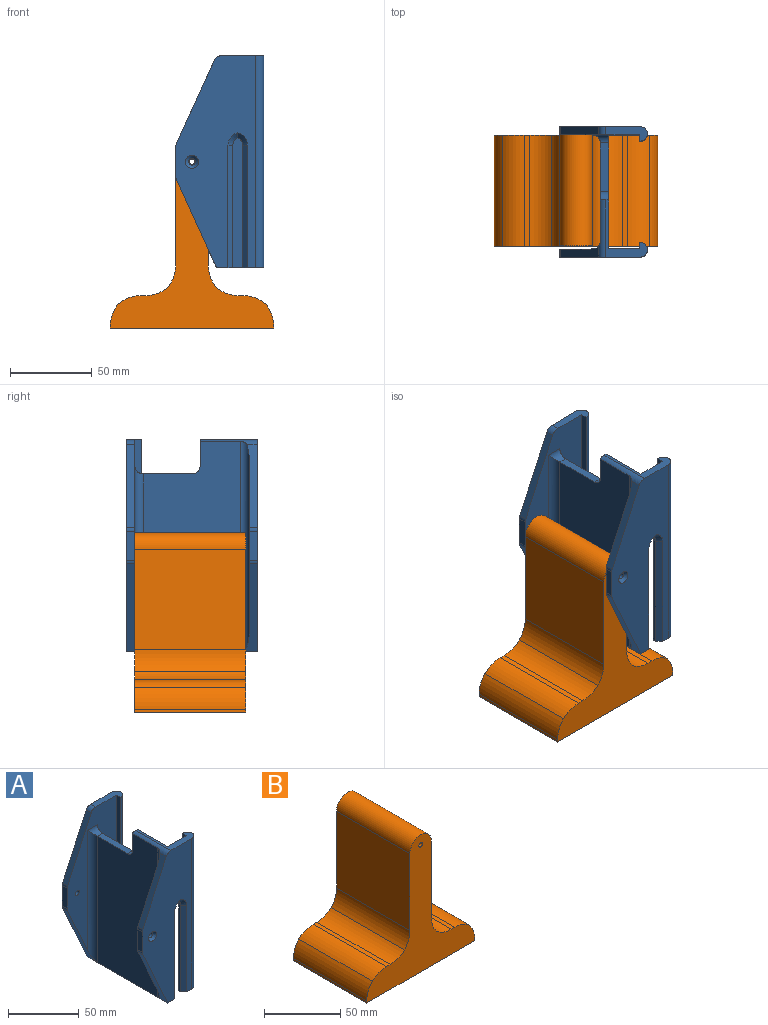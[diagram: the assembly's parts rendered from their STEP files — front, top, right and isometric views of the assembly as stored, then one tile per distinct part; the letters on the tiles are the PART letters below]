
ASSEMBLY  parts=2 mates=1
PART A: 47 faces, bbox 54.7x80.8x130.8 mm
  f0: plane 80x28.98mm, normal (0,0,-1), area 549.8mm2, adj f1,f3,f6,f9,f11,f12,f13,f16
  f1: plane 130x19mm, normal (0,1,0), area 2000.2mm2, adj f0,f7,f8,f11,f14,f23,f24,f25
  f2: plane 25.76x9mm, normal (0,0,1), area 138.2mm2, adj f6,f12,f13,f35,f39,f40
  f3: plane 128.83x60mm, normal (-1,0,0), area 7041mm2, adj f0,f21,f22,f27,f29,f30,f31
  f4: plane 17.83x5mm, normal (-1,0,0), area 89.2mm2, adj f9,f10,f32,f33
  f5: plane 17.83x5mm, normal (-1,0,0), area 89.2mm2, adj f6,f12,f34,f36
  f6: plane 130x49mm, normal (0,1,0), area 4942.8mm2, adj f0,f2,f5,f16,f17,f34,f35,f36
  f7: plane 35x25.76mm, normal (0,0,1), area 191.6mm2, adj f1,f9,f11,f14,f22,f31,f37,f38
  f8: plane 12.98x9mm, normal (0,0,-1), area 69.8mm2, adj f1,f9,f14,f24,f37,f38,f43
  f9: plane 130x49mm, normal (0,-1,0), area 3973.9mm2, adj f0,f4,f7,f8,f19,f20,f31,f32
  f10: plane 108x20mm, normal (0,1,0), area 1267.3mm2, adj f4,f18,f19,f20,f30,f32,f33
  f11: plane 130x70mm, normal (1,0,0), area 8270.7mm2, adj f0,f1,f7,f12,f21,f22,f28,f29
  f12: plane 130x49mm, normal (0,-1,0), area 3868mm2, adj f0,f2,f5,f11,f13,f15,f16,f17
  f13: plane 130x4mm, normal (-1,0,0), area 520mm2, adj f0,f2,f12,f40
  f14: plane 130x4mm, normal (-1,0,0), area 520mm2, adj f1,f7,f8,f38
  f15: cylinder r=2mm len=4mm, axis (0,-1,0), area 37.7mm2, adj f12,f45
  f16: plane 54.01x24.55mm, normal (-0.91,0,-0.41), area 309.6mm2, adj f0,f6,f12,f27,f34
  f17: plane 51.08x23.22mm, normal (-0.91,0,0.41), area 280.6mm2, adj f6,f12,f35,f36
  f18: cylinder r=2mm len=4mm, axis (0,-1,0), area 37.7mm2, adj f10,f46
  f19: plane 54.01x24.55mm, normal (-0.91,0,-0.41), area 309.6mm2, adj f0,f9,f10,f30,f33
  f20: plane 51.84x23.97mm, normal (-0.91,0,0.41), area 284.9mm2, adj f9,f10,f30,f31,f32
  f21: plane 30x5mm, normal (0,0,1), area 150mm2, adj f3,f11,f28,f29
  f22: plane 16x5mm, normal (0,1,0), area 78.8mm2, adj f3,f7,f11,f29,f31
  f23: plane 75x2mm, normal (1,0,0), area 150mm2, adj f0,f1,f26,f41
  f24: plane 75x2mm, normal (-1,0,0), area 150mm2, adj f1,f8,f25,f43
  f25: cylinder r=5mm len=4.58mm, axis (0,1,0), area 11.6mm2, adj f1,f24,f26,f44
  f26: cylinder r=5mm len=4.58mm, axis (0,-1,0), area 11.6mm2, adj f1,f23,f25,f42
  f27: cylinder r=5mm len=114mm, axis (0,0,1), area 839mm2, adj f3,f12,f16,f28
  f28: cylinder r=5mm len=10mm, axis (1,0,0), area 53.5mm2, adj f11,f12,f21,f27
  f29: cylinder r=5mm len=5mm, axis (1,0,0), area 39.3mm2, adj f3,f11,f21,f22
  f30: cylinder r=5mm len=128.83mm, axis (0,0,1), area 953.3mm2, adj f3,f10,f19,f20,f31
  f31: cylinder r=5mm len=35mm, axis (0,1,0), area 140.9mm2, adj f3,f7,f9,f20,f22,f30
  f32: cylinder r=5mm len=5mm, axis (0,1,0), area 10.7mm2, adj f4,f9,f10,f20
  f33: cylinder r=5mm len=5mm, axis (0,-1,0), area 10.7mm2, adj f4,f9,f10,f19
  f34: cylinder r=5mm len=5mm, axis (0,-1,0), area 10.7mm2, adj f5,f6,f12,f16
  f35: cylinder r=5mm len=5mm, axis (0,1,0), area 28.6mm2, adj f2,f6,f12,f17
  f36: cylinder r=5mm len=5mm, axis (0,1,0), area 10.7mm2, adj f5,f6,f12,f17
  f37: cylinder r=5mm len=130mm, axis (0,0,-1), area 955.9mm2, adj f7,f8,f9,f38
  f38: cylinder r=5mm len=130mm, axis (0,0,-1), area 955.9mm2, adj f7,f8,f14,f37
  f39: cylinder r=5mm len=130mm, axis (0,0,-1), area 955.9mm2, adj f0,f2,f6,f40
  f40: cylinder r=5mm len=130mm, axis (0,0,-1), area 955.9mm2, adj f0,f2,f13,f39
  f41: plane 75x3mm, normal (0.71,-0.71,0), area 318.2mm2, adj f0,f9,f23,f42
  f42: cone r=8mm half-angle=45deg, axis (0,-1,0), area 34.3mm2, adj f9,f26,f41,f44
  f43: plane 75x3mm, normal (-0.71,-0.71,0), area 318.2mm2, adj f8,f9,f24,f44
  f44: cone r=8mm half-angle=45deg, axis (0,-1,0), area 34.3mm2, adj f9,f25,f42,f43
  f45: cone r=4mm half-angle=45deg, axis (0,1,0), area 53.3mm2, adj f6,f15
  f46: cone r=4mm half-angle=45deg, axis (0,-1,0), area 53.3mm2, adj f9,f18
PART B: 19 faces, bbox 100x68x110 mm
  f0: plane 68x61.72mm, normal (1,0,0), area 4196.7mm2, adj f8,f9,f10,f16
  f1: plane 68x61.72mm, normal (-1,0,0), area 4196.7mm2, adj f8,f9,f10,f12
  f2: plane 68x3.43mm, normal (0,0,1), area 233.3mm2, adj f8,f9,f11,f14
  f3: plane 68x1.72mm, normal (-1,0,0), area 116.7mm2, adj f4,f8,f9,f13
  f4: plane 100x68mm, normal (0,0,-1), area 6800mm2, adj f3,f5,f8,f9
  f5: plane 68x1.72mm, normal (1,0,0), area 116.7mm2, adj f4,f8,f9,f18
  f6: plane 68x3.43mm, normal (0,0,1), area 233.3mm2, adj f8,f9,f15,f17
  f7: cylinder r=1.75mm len=68mm, axis (0,1,0), area 747.7mm2, adj f8,f9
  f8: plane 110x100mm, normal (0,-1,0), area 3747.5mm2, adj f0,f1,f2,f3,f4,f5,f6,f7
  f9: plane 110x100mm, normal (0,1,0), area 3747.5mm2, adj f0,f1,f2,f3,f4,f5,f6,f7
  f10: cylinder r=10mm len=68mm, axis (0,1,0), area 2136.3mm2, adj f0,f1,f8,f9
  f11: cylinder r=20mm len=68mm, axis (0,-1,0), area 985.6mm2, adj f2,f8,f9,f12
  f12: cylinder r=20mm len=68mm, axis (0,-1,0), area 985.6mm2, adj f1,f8,f9,f11
  f13: cylinder r=20mm len=68mm, axis (0,1,0), area 985.6mm2, adj f3,f8,f9,f14
  f14: cylinder r=20mm len=68mm, axis (0,1,0), area 985.6mm2, adj f2,f8,f9,f13
  f15: cylinder r=20mm len=68mm, axis (0,-1,0), area 985.6mm2, adj f6,f8,f9,f16
  f16: cylinder r=20mm len=68mm, axis (0,1,0), area 985.6mm2, adj f0,f8,f9,f15
  f17: cylinder r=20mm len=68mm, axis (0,1,0), area 985.6mm2, adj f6,f8,f9,f18
  f18: cylinder r=20mm len=68mm, axis (0,-1,0), area 985.6mm2, adj f5,f8,f9,f17
PLACE A t=(-55.24,-32.28,37.68)mm
PLACE B t=(-58.66,2.72,0.68)mm
MATE slider A.f15 <-> B.f7  axis (0,-1,0) through (-108.66,2.72,102.68)mm
